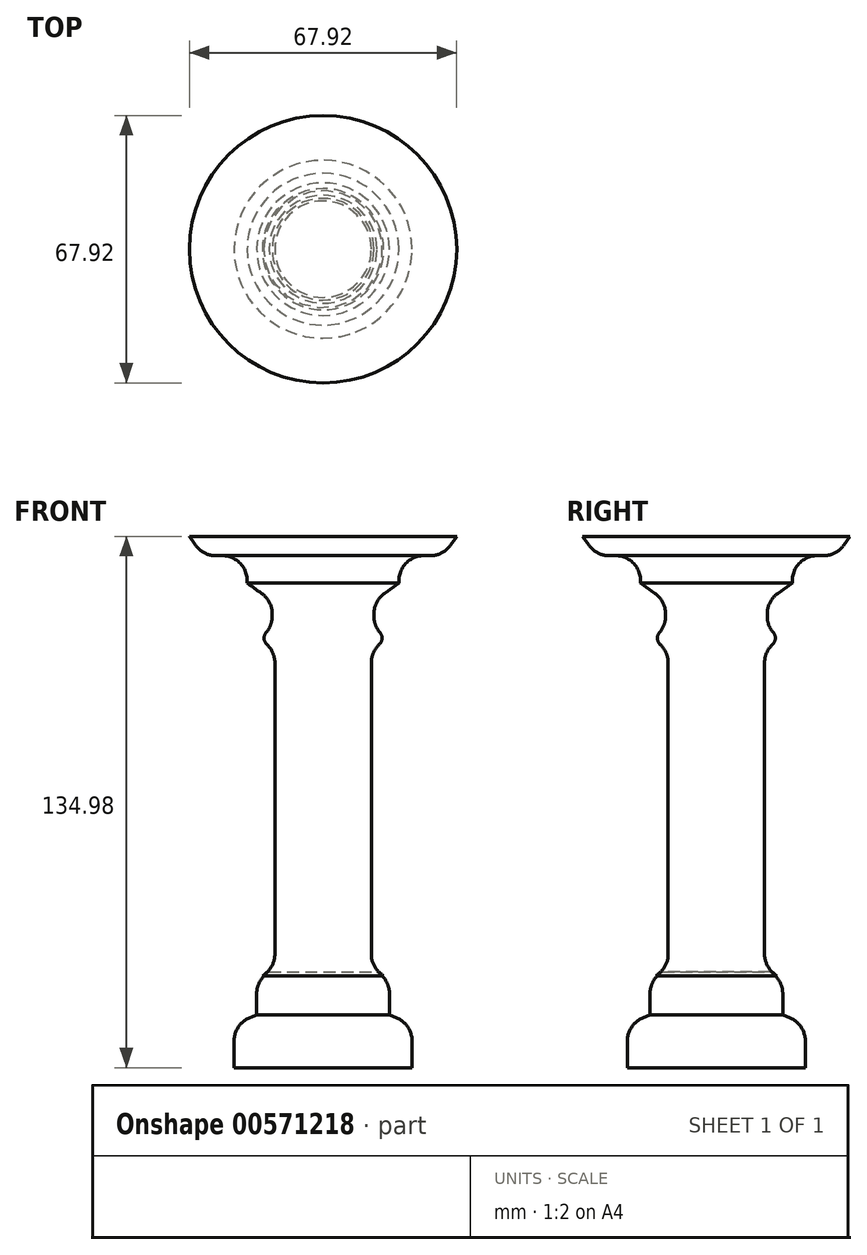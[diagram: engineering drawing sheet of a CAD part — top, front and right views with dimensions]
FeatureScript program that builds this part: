
annotation { "Feature Type Name" : "Feature", "Feature Type Description" : "" }
export const myFeature = defineFeature(function(context is Context, id is Id, definition is map)
    precondition{}
    {
        {
            var Q0;
            Q0=qCreatedBy(makeId("Front.planeOp"),FACE);
            var sketch = newSketch(context, id + "F0", { "sketchPlane" : qUnion([Q0])});
            skLineSegment(sketch, "E0", {"start": v(-12.25, 32.94) * mm, "end": v(-12.25, -41.1) * mm});
            skLineSegment(sketch, "E1", {"start": v(-13.7, -45.6) * mm, "end": v(-15.4, -46.58) * mm});
            skLineSegment(sketch, "E2", {"start": v(-16.85, -51.08) * mm, "end": v(-16.85, -56.55) * mm});
            skLineSegment(sketch, "E3", {"start": v(-16.85, -56.55) * mm, "end": v(-18.67, -57.3) * mm});
            skLineSegment(sketch, "E4", {"start": v(-22.6, -63.17) * mm, "end": v(-22.6, -69.94) * mm});
            skLineSegment(sketch, "E5", {"start": v(0, -69.94) * mm, "end": v(0, 56.12) * mm});
            skLineSegment(sketch, "E6", {"start": v(-12.92, 44.74) * mm, "end": v(-12.92, 45.37) * mm});
            skLineSegment(sketch, "E7", {"start": v(-15.6, 50.55) * mm, "end": v(-19.28, 53.17) * mm});
            skLineSegment(sketch, "E8", {"start": v(-19.28, 53.17) * mm, "end": v(-19.28, 53.8) * mm});
            skLineSegment(sketch, "E9", {"start": v(-25.63, 60.15) * mm, "end": v(-27.22, 60.15) * mm});
            skLineSegment(sketch, "E10", {"start": v(-32.4, 62.84) * mm, "end": v(-33.96, 65.04) * mm});
            skLineSegment(sketch, "E11", {"start": v(-33.96, 65.04) * mm, "end": v(0, 65.04) * mm});
            skLineSegment(sketch, "E12", {"start": v(0, 65.04) * mm, "end": v(0, 56.12) * mm});
            skLineSegment(sketch, "E13", {"start": v(-22.6, -69.94) * mm, "end": v(0, -69.94) * mm});
            skPoint(sketch, "E14.visualSharp", {"position": v(-19.28, 60.15) * mm});
            skArc(sketch, "E14.filletArc", {"start": v(-19.28, 53.8) * mm, "mid": v(-21.14, 58.3) * mm, "end": v(-25.63, 60.15) * mm});
            skPoint(sketch, "E15.visualSharp", {"position": v(-12.92, 48.65) * mm});
            skArc(sketch, "E15.filletArc", {"start": v(-12.92, 45.37) * mm, "mid": v(-13.63, 48.28) * mm, "end": v(-15.6, 50.55) * mm});
            skPoint(sketch, "E16.visualSharp", {"position": v(-12.25, -44.75) * mm});
            skArc(sketch, "E16.filletArc", {"start": v(-15.4, -46.58) * mm, "mid": v(-13.1, -44.26) * mm, "end": v(-12.25, -41.1) * mm});
            skPoint(sketch, "E17.visualSharp", {"position": v(-16.85, -47.43) * mm});
            skArc(sketch, "E17.filletArc", {"start": v(-13.7, -45.6) * mm, "mid": v(-16, -47.91) * mm, "end": v(-16.85, -51.08) * mm});
            skPoint(sketch, "E18.visualSharp", {"position": v(-22.6, -58.9) * mm});
            skArc(sketch, "E18.filletArc", {"start": v(-18.67, -57.3) * mm, "mid": v(-21.53, -59.63) * mm, "end": v(-22.6, -63.17) * mm});
            skPoint(sketch, "E19.visualSharp", {"position": v(-30.5, 60.15) * mm});
            skArc(sketch, "E19.filletArc", {"start": v(-32.4, 62.84) * mm, "mid": v(-30.14, 60.86) * mm, "end": v(-27.22, 60.15) * mm});
            skArc(sketch, "E20", {"start": v(-14.47, 40.59) * mm, "mid": v(-14.99, 39.07) * mm, "end": v(-14.3, 37.61) * mm});
            skPoint(sketch, "E21.visualSharp", {"position": v(-12.25, 37.14) * mm});
            skArc(sketch, "E21.filletArc", {"start": v(-12.25, 32.94) * mm, "mid": v(-12.78, 35.5) * mm, "end": v(-14.3, 37.61) * mm});
            skPoint(sketch, "E22.visualSharp", {"position": v(-12.92, 41.32) * mm});
            skArc(sketch, "E22.filletArc", {"start": v(-14.47, 40.59) * mm, "mid": v(-13.32, 42.52) * mm, "end": v(-12.92, 44.74) * mm});
            skSolve(sketch);
        }
        {
            var Q0;
            Q0=makeQuery(id+"F0.imprint","IMPRINT",FACE,{"disambiguationData":[TD([[makeQuery(id+"F0.imprint","IMPRINT",EDGE,{"derivedFrom":sQuery(id+"F0.wireOp",EDGE,"E0")}),1.0]])]});
            var Q1;
            Q1=sQuery(id+"F0.wireOp",EDGE,"E5");
            revolve(context, id + "F1", {"entities" : qUnion([Q0]), "axis" : qUnion([Q1]), "revolveType" : RevolveType.FULL});
        }
    });
